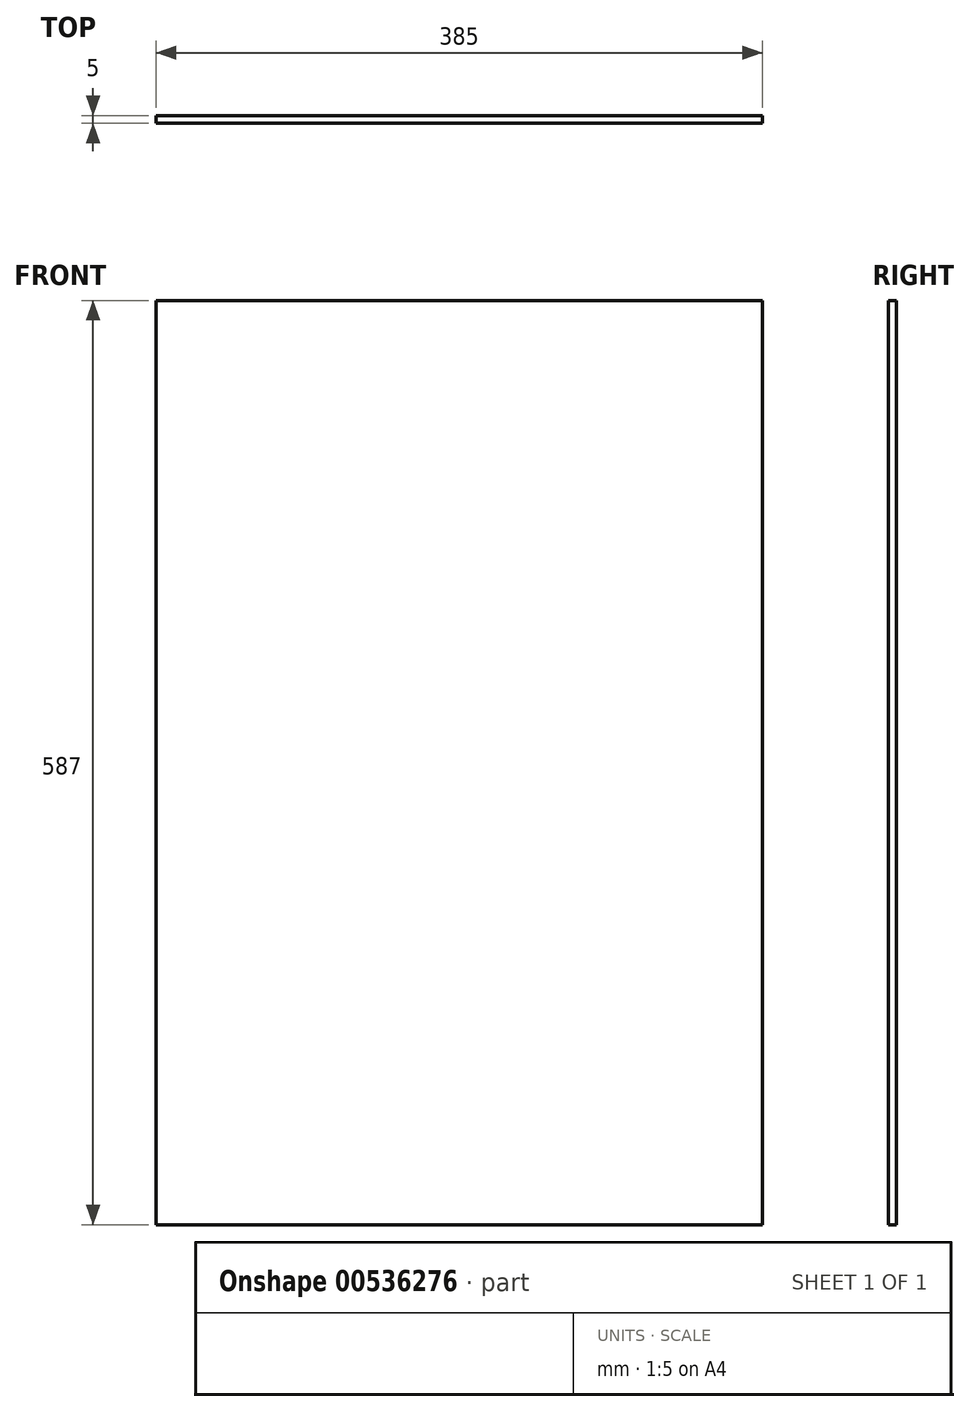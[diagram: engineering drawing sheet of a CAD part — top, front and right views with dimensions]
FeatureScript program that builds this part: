
annotation { "Feature Type Name" : "Feature", "Feature Type Description" : "" }
export const myFeature = defineFeature(function(context is Context, id is Id, definition is map)
    precondition{}
    {
        {
            var Q0;
            Q0=qCreatedBy(makeId("Front.planeOp"),FACE);
            var sketch = newSketch(context, id + "F0", { "sketchPlane" : qUnion([Q0])});
            skLineSegment(sketch, "E0.bottom", {"start": v(-192.5, 293.5) * mm, "end": v(192.5, 293.5) * mm});
            skLineSegment(sketch, "E0.top", {"start": v(-192.5, -293.5) * mm, "end": v(192.5, -293.5) * mm});
            skLineSegment(sketch, "E0.left", {"start": v(-192.5, 293.5) * mm, "end": v(-192.5, -293.5) * mm});
            skLineSegment(sketch, "E0.right", {"start": v(192.5, 293.5) * mm, "end": v(192.5, -293.5) * mm});
            skPoint(sketch, "E0.middle", {"position": v(0, 0) * mm});
            skSolve(sketch);
        }
        {
            var Q0;
            Q0=makeQuery(id+"F0.imprint","IMPRINT",FACE,{"disambiguationData":[TD([[makeQuery(id+"F0.imprint","IMPRINT",EDGE,{"derivedFrom":sQuery(id+"F0.wireOp",EDGE,"E0.bottom")}),-1.0]])]});
            extrude(context, id + "F1", {"entities" : qUnion([Q0]), "depth" : 0.5 * mm, "offsetDistance" : 25 * mm});
        }
        {
            var Q0;
            Q0=makeQuery(id+"F0.imprint","IMPRINT",FACE,{"disambiguationData":[TD([[makeQuery(id+"F0.imprint","IMPRINT",EDGE,{"derivedFrom":sQuery(id+"F0.wireOp",EDGE,"E0.bottom")}),-1.0]])]});
            extrude(context, id + "F2", {"entities" : qUnion([Q0]), "operationType" : NewBodyOperationType.ADD, "depth" : 5 * mm, "offsetDistance" : 25 * mm});
        }
    });
